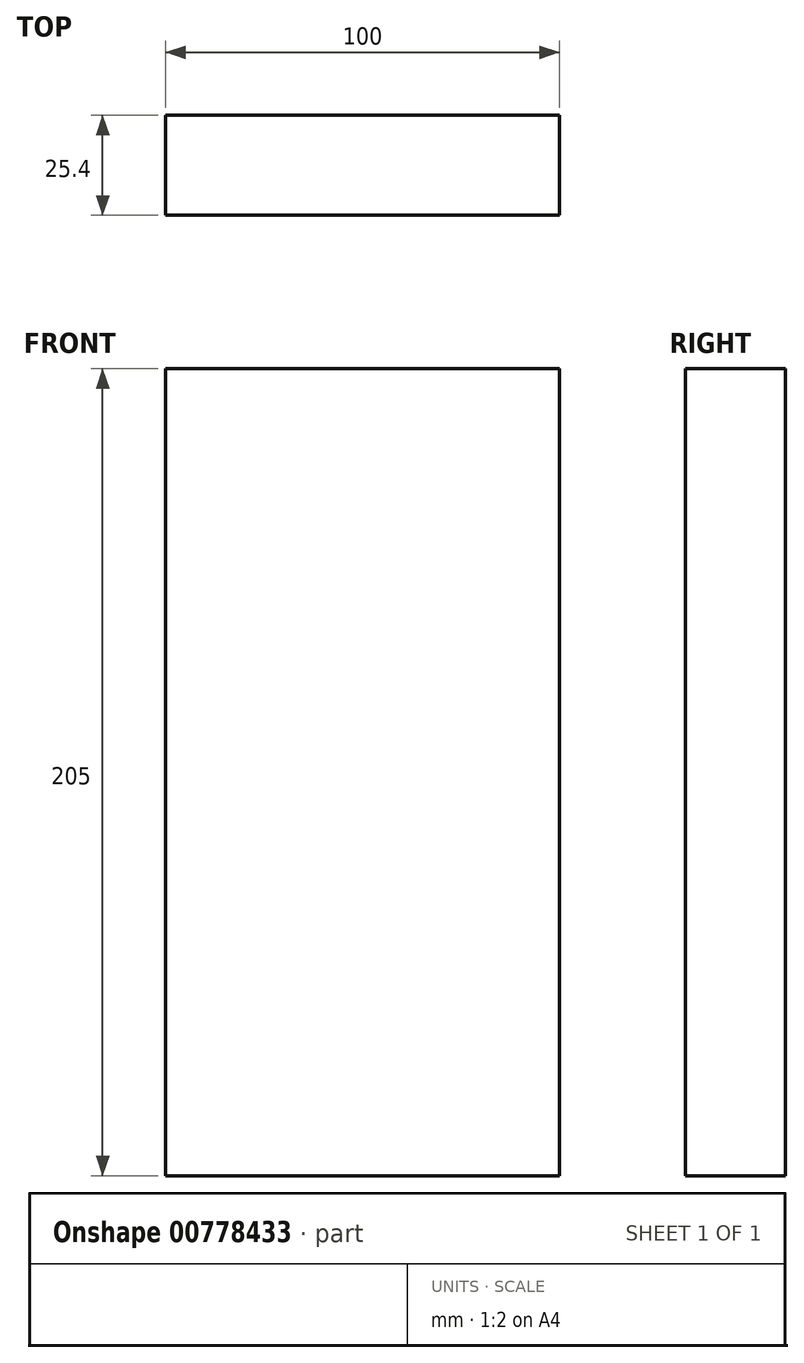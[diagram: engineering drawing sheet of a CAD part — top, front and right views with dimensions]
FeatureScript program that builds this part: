
annotation { "Feature Type Name" : "Feature", "Feature Type Description" : "" }
export const myFeature = defineFeature(function(context is Context, id is Id, definition is map)
    precondition{}
    {
        {
            var Q0;
            Q0=qCreatedBy(makeId("Front.planeOp"),FACE);
            var sketch = newSketch(context, id + "F0", { "sketchPlane" : qUnion([Q0])});
            skLineSegment(sketch, "E0.bottom", {"start": v(-60.6, 96.82) * mm, "end": v(39.4, 96.82) * mm});
            skLineSegment(sketch, "E0.top", {"start": v(-60.6, -108.18) * mm, "end": v(39.4, -108.18) * mm});
            skLineSegment(sketch, "E0.left", {"start": v(-60.6, 96.82) * mm, "end": v(-60.6, -108.18) * mm});
            skLineSegment(sketch, "E0.right", {"start": v(39.4, 96.82) * mm, "end": v(39.4, -108.18) * mm});
            skSolve(sketch);
        }
        {
            var Q0;
            Q0 = qSketchRegion(id + "F0", true);
            var Q1;
            Q1=makeQuery(id+"F0.imprint","IMPRINT",FACE,{"disambiguationData":[TD([[makeQuery(id+"F0.imprint","IMPRINT",EDGE,{"derivedFrom":sQuery(id+"F0.wireOp",EDGE,"E0.bottom")}),-1.0]])]});
            extrude(context, id + "F1", {"entities" : qUnion([Q0, Q1]), "depth" : 25.4 * mm, "offsetDistance" : 25.4 * mm});
        }
    });
